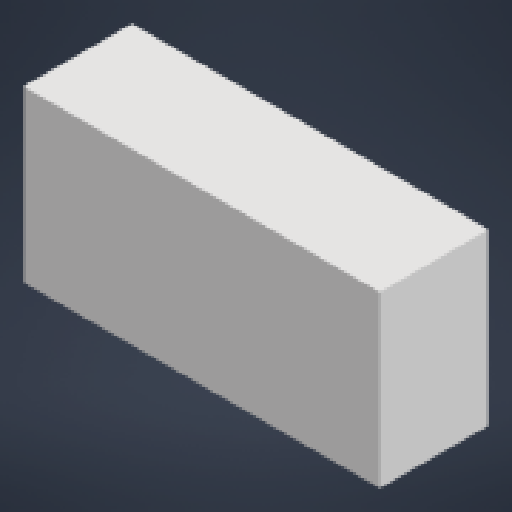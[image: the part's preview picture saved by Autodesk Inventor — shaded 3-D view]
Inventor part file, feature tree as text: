
AUTODESK INVENTOR PART (.ipt)
format: ipt  version: 2023 (Build 270158000, 158)  size: 168,448 bytes
history: native  units: in
note: dims shown in document units (in); Inventor stores cm internally (conversion verified against a paired STEP export)
features: extrude x4, sketch x3, direct_edit x1, move_body x1
ambient origin geometry x8: Origin, YZ Plane, XZ Plane, XY Plane, X Axis, Y Axis, Z Axis, Center Point
bodies: Solid1 (feature_tree)
feature tree (9):
  extrude  "Extrusion1"  Depth=0.1969in
  sketch  "Sketch2"  dims[d2=0.126in d3=0.0in d4=0.063in]
  extrude  "Extrusion2"  Depth=0.126in
  extrude  "Extrusion3"  Depth=0.0039in
  direct_edit  "Direct Edit1"
  extrude  "Extrusion4"  Depth=0.0591in TaperAngle=0.0deg
  sketch  "Sketch1"  dims[d0=0.4134in d1=0.1969in]
  sketch  "Sketch3"  dims[d5=0.1024in d6=0.1575in d7=0.0591in d8=0.0in d9=0.0in d10=0.0in d11=0.0in d12=0.0in d13=-0.0276in d14=0.3583in d15=0.122in d16=0.0197in d17=0.0197in d18=0.1457in d19=0.0197in d20=0.0394in d21=0.1457in d22=0.0197in d23=0.0394in d24=0.0039in d25=0.0in]
  move_body  "Move1"
